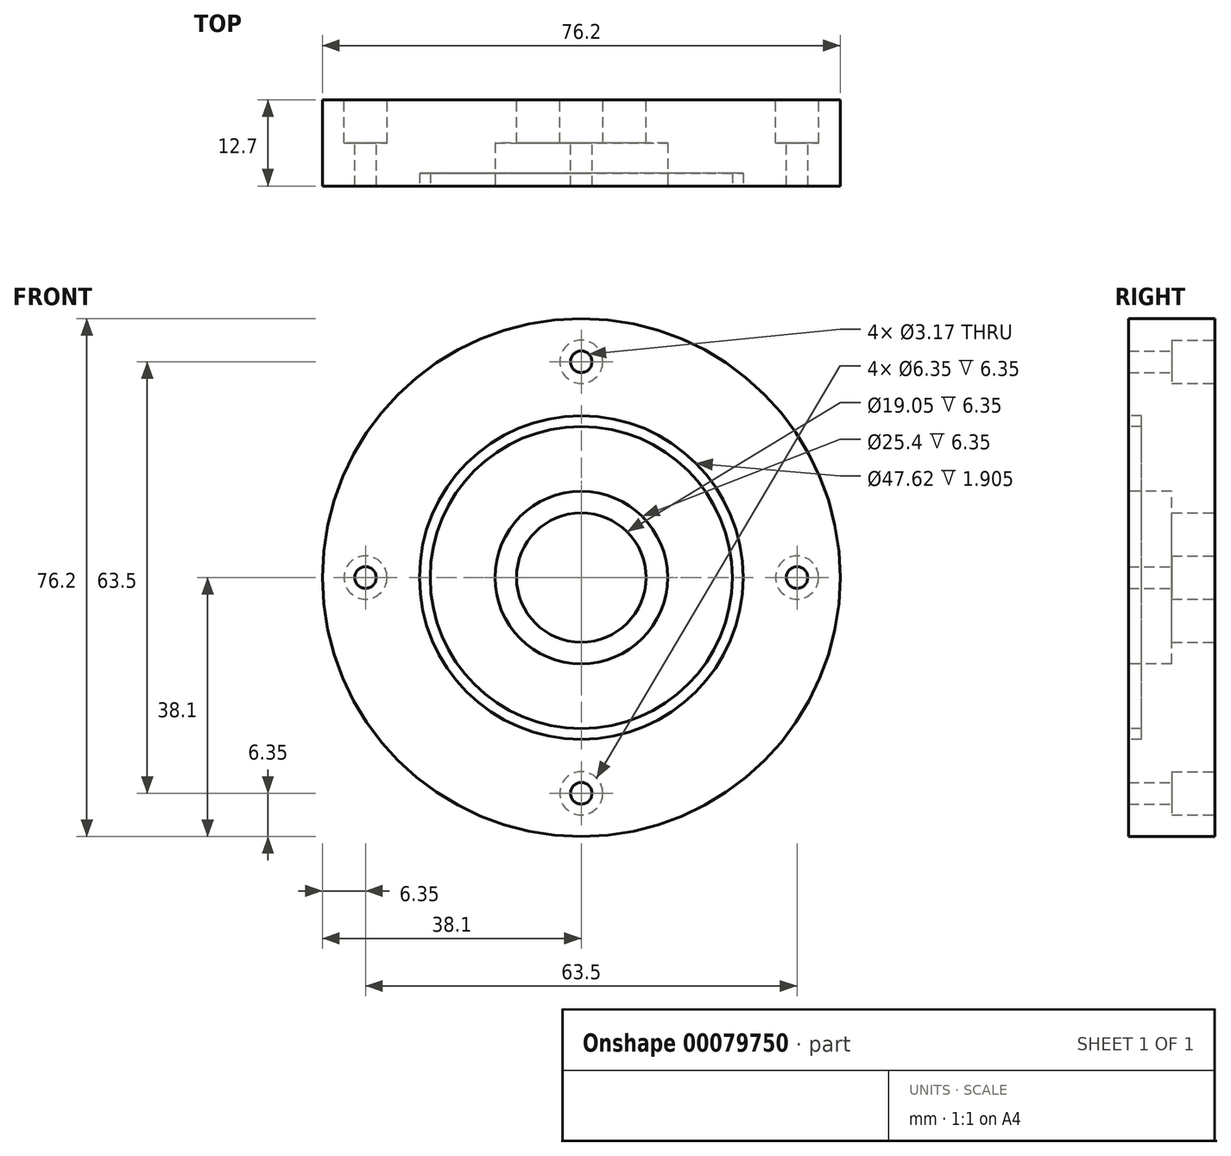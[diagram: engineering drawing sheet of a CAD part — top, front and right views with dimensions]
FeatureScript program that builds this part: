
annotation { "Feature Type Name" : "Feature", "Feature Type Description" : "" }
export const myFeature = defineFeature(function(context is Context, id is Id, definition is map)
    precondition{}
    {
        {
            var Q0;
            Q0=qCreatedBy(makeId("Front.planeOp"),FACE);
            var sketch = newSketch(context, id + "F0", { "sketchPlane" : qUnion([Q0])});
            skCircle(sketch, "E0", {"center": v(0, 0) * mm, "radius": 38.1 * mm});
            skCircle(sketch, "E1", {"center": v(0, 0) * mm, "radius": 9.53 * mm});
            skSolve(sketch);
        }
        {
            var Q0;
            Q0 = qSketchRegion(id + "F0", true);
            extrude(context, id + "F1", {"entities" : qUnion([Q0]), "depth" : 12.7 * mm});
        }
        {
            var Q0;
            Q0=makeQuery(id+"F1.opExtrude","CAP_FACE",FACE,{"disambiguationData":[OSD([sQuery(id+"F0.wireOp",EDGE,"E0"),sQuery(id+"F0.wireOp",EDGE,"E1")])],"isStart":false});
            var sketch = newSketch(context, id + "F2", { "sketchPlane" : qUnion([Q0])});
            skCircle(sketch, "E2", {"center": v(0, 0) * mm, "radius": 12.7 * mm});
            skSolve(sketch);
        }
        {
            var Q0;
            Q0=makeQuery(id+"F2.imprint","IMPRINT",FACE,{"disambiguationData":[TD([[makeQuery(id+"F2.imprint","IMPRINT",EDGE,{"derivedFrom":sQuery(id+"F2.wireOp",EDGE,"E2")}),1.0]])]});
            extrude(context, id + "F3", {"entities" : qUnion([Q0]), "operationType" : NewBodyOperationType.REMOVE, "oppositeDirection" : true, "depth" : 6.35 * mm});
        }
        {
            var Q0;
            Q0=makeQuery(id+"F1.opExtrude","CAP_FACE",FACE,{"disambiguationData":[OSD([sQuery(id+"F0.wireOp",EDGE,"E0"),sQuery(id+"F0.wireOp",EDGE,"E1")])],"isStart":true});
            var sketch = newSketch(context, id + "F4", { "sketchPlane" : qUnion([Q0])});
            skPoint(sketch, "E3", {"position": v(0, 31.75) * mm});
            skPoint(sketch, "E4", {"position": v(-31.75, 0) * mm});
            skPoint(sketch, "E5", {"position": v(0, -31.75) * mm});
            skPoint(sketch, "E6", {"position": v(31.75, 0) * mm});
            skSolve(sketch);
        }
        {
            var Q0;
            Q0=sQuery(id+"F4.wireOp",VERTEX,"E3");
            var Q1;
            Q1=sQuery(id+"F4.wireOp",VERTEX,"E4");
            var Q2;
            Q2=sQuery(id+"F4.wireOp",VERTEX,"E5");
            var Q3;
            Q3=sQuery(id+"F4.wireOp",VERTEX,"E6");
            var Q4;
            Q4=makeQuery(id+"F1.opExtrude","SWEPT_BODY",BODY,{"disambiguationData":[OSD([sQuery(id+"F0.wireOp",EDGE,"E0"),sQuery(id+"F0.wireOp",EDGE,"E1")])]});
            hole(context, id + "F5", {"style" : HoleStyle.C_BORE, "endStyle" : HoleEndStyle.THROUGH, "holeDiameter" : 3.17 * mm, "cBoreDiameter" : 6.35 * mm, "cBoreDepth" : 6.35 * mm, "locations" : qUnion([Q0, Q1, Q2, Q3]), "scope" : qUnion([Q4]), "isTappedThrough" : true});
        }
        {
            var Q0;
            Q0=makeQuery(id+"F1.opExtrude","CAP_FACE",FACE,{"disambiguationData":[OSD([sQuery(id+"F0.wireOp",EDGE,"E0"),sQuery(id+"F0.wireOp",EDGE,"E1")])],"isStart":false});
            var sketch = newSketch(context, id + "F6", { "sketchPlane" : qUnion([Q0])});
            skCircle(sketch, "E7", {"center": v(0, 0) * mm, "radius": 22.23 * mm});
            skCircle(sketch, "E8", {"center": v(0, 0) * mm, "radius": 23.81 * mm});
            skSolve(sketch);
        }
        {
            var Q0;
            Q0=makeQuery(id+"F6.imprint","IMPRINT",FACE,{"disambiguationData":[TD([[makeQuery(id+"F6.imprint","IMPRINT",EDGE,{"derivedFrom":sQuery(id+"F6.wireOp",EDGE,"E7")}),-1.0]])]});
            extrude(context, id + "F7", {"entities" : qUnion([Q0]), "operationType" : NewBodyOperationType.REMOVE, "oppositeDirection" : true, "depth" : 1.9 * mm});
        }
    });
